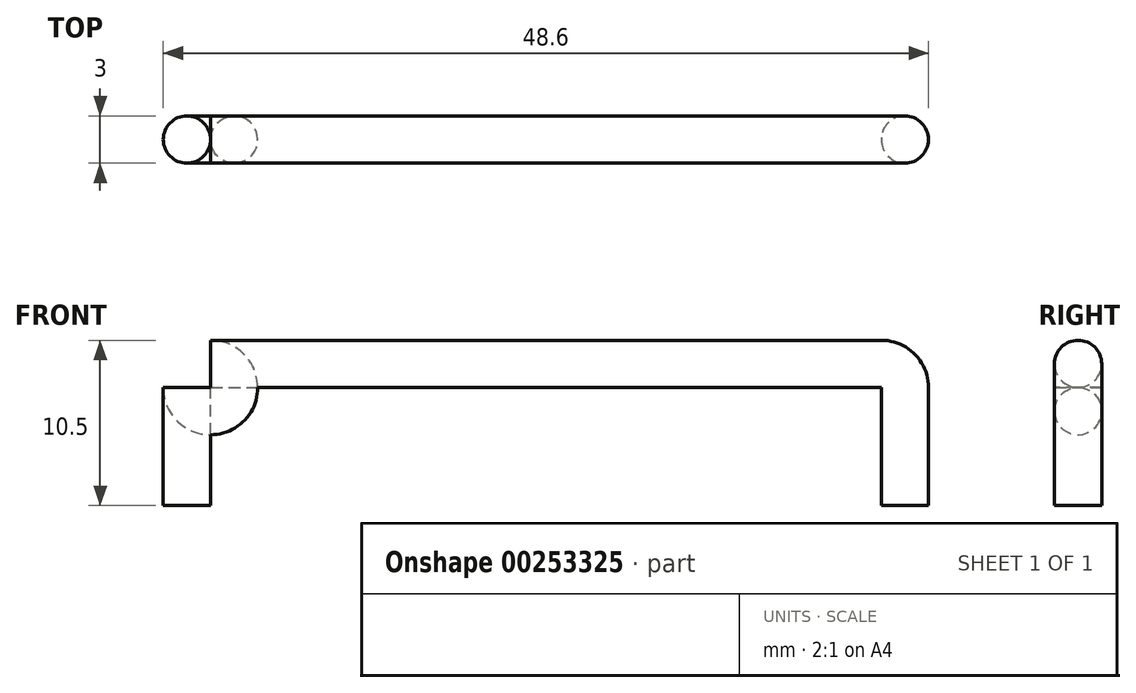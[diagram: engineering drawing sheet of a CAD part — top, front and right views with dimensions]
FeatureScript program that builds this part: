
annotation { "Feature Type Name" : "Feature", "Feature Type Description" : "" }
export const myFeature = defineFeature(function(context is Context, id is Id, definition is map)
    precondition{}
    {
        {
            var Q0;
            Q0=qCreatedBy(makeId("Front.planeOp"),FACE);
            var sketch = newSketch(context, id + "F0", { "sketchPlane" : qUnion([Q0])});
            skLineSegment(sketch, "E0", {"start": v(-21.3, 0) * mm, "end": v(21.3, 0) * mm});
            skLineSegment(sketch, "E1", {"start": v(22.8, -1.5) * mm, "end": v(22.8, -9) * mm});
            skLineSegment(sketch, "E2.MirrorCS", {"start": v(-22.8, -1.5) * mm, "end": v(-22.8, -9) * mm});
            skArc(sketch, "E3", {"start": v(22.8, -1.5) * mm, "mid": v(22.36, -0.44) * mm, "end": v(21.3, 0) * mm});
            skArc(sketch, "E4.MirrorCS", {"start": v(-22.8, -1.5) * mm, "mid": v(-22.36, -0.44) * mm, "end": v(-21.3, 0) * mm});
            skSolve(sketch);
        }
        {
            var Q0;
            Q0=sQuery(id+"F0.wireOp",EDGE,"E2.MirrorCS");
            var Q1;
            Q1=sQuery(id+"F0.wireOp",VERTEX,"E2.MirrorCS.end");
            cPlane(context, id + "F1", {"entities" : qUnion([Q0, Q1]), "cplaneType" : CPlaneType.CURVE_POINT, "offset" : 25 * mm, "width" : 150 * mm, "height" : 150 * mm});
        }
        {
            var Q0;
            Q0=qCreatedBy(id+"F1.planeOp",FACE);
            var sketch = newSketch(context, id + "F2", { "sketchPlane" : qUnion([Q0])});
            skPoint(sketch, "E5.0", {"position": v(-22.8, 0) * mm});
            skCircle(sketch, "E6", {"center": v(-22.8, 0) * mm, "radius": 1.5 * mm});
            skSolve(sketch);
        }
        {
            var Q0;
            Q0=makeQuery(id+"F2.imprint","IMPRINT",FACE,{"disambiguationData":[TD([[makeQuery(id+"F2.imprint","IMPRINT",EDGE,{"derivedFrom":sQuery(id+"F2.wireOp",EDGE,"E6")}),1.0]])]});
            var Q1;
            Q1=sQuery(id+"F0.wireOp",EDGE,"E2.MirrorCS");
            var Q2;
            Q2=sQuery(id+"F0.wireOp",EDGE,"E4.MirrorCS");
            var Q3;
            Q3=sQuery(id+"F0.wireOp",EDGE,"E0");
            var Q4;
            Q4=sQuery(id+"F0.wireOp",EDGE,"E3");
            var Q5;
            Q5=sQuery(id+"F0.wireOp",EDGE,"E1");
            sweep(context, id + "F3", {"profiles" : qUnion([Q0]), "path" : qUnion([Q1, Q2, Q3, Q4, Q5])});
        }
    });
